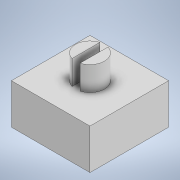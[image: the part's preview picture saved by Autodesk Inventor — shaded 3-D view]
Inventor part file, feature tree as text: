
AUTODESK INVENTOR PART (.ipt)
format: ipt  version: 2022 (Build 260153000, 153)  size: 111,616 bytes
history: native  units: in
note: dims shown in document units (in); Inventor stores cm internally (conversion verified against a paired STEP export)
features: extrude x3, sketch x3, projected_geometry x2
ambient origin geometry x8: Origin, YZ Plane, XZ Plane, XY Plane, X Axis, Y Axis, Z Axis, Center Point
bodies: Solid1 (feature_tree)
feature tree (8):
  extrude  "Extrusion1"  Depth=0.3839in
  extrude  "Extrusion2"  Depth=0.1969in
  extrude  "Extrusion3"  Depth=0.0394in
  sketch  "Sketch1"  dims[d0=0.3839in d1=0.3839in]
  sketch  "Sketch2"  dims[d2=0.1969in d3=0.0in d4=0.1417in]
  projected_geometry  "Projected Loop1"
  sketch  "Sketch3"  dims[d5=0.1181in d6=0.0in d7=0.0394in d8=0.1181in d9=0.0in]
  projected_geometry  "Projected Loop2"
